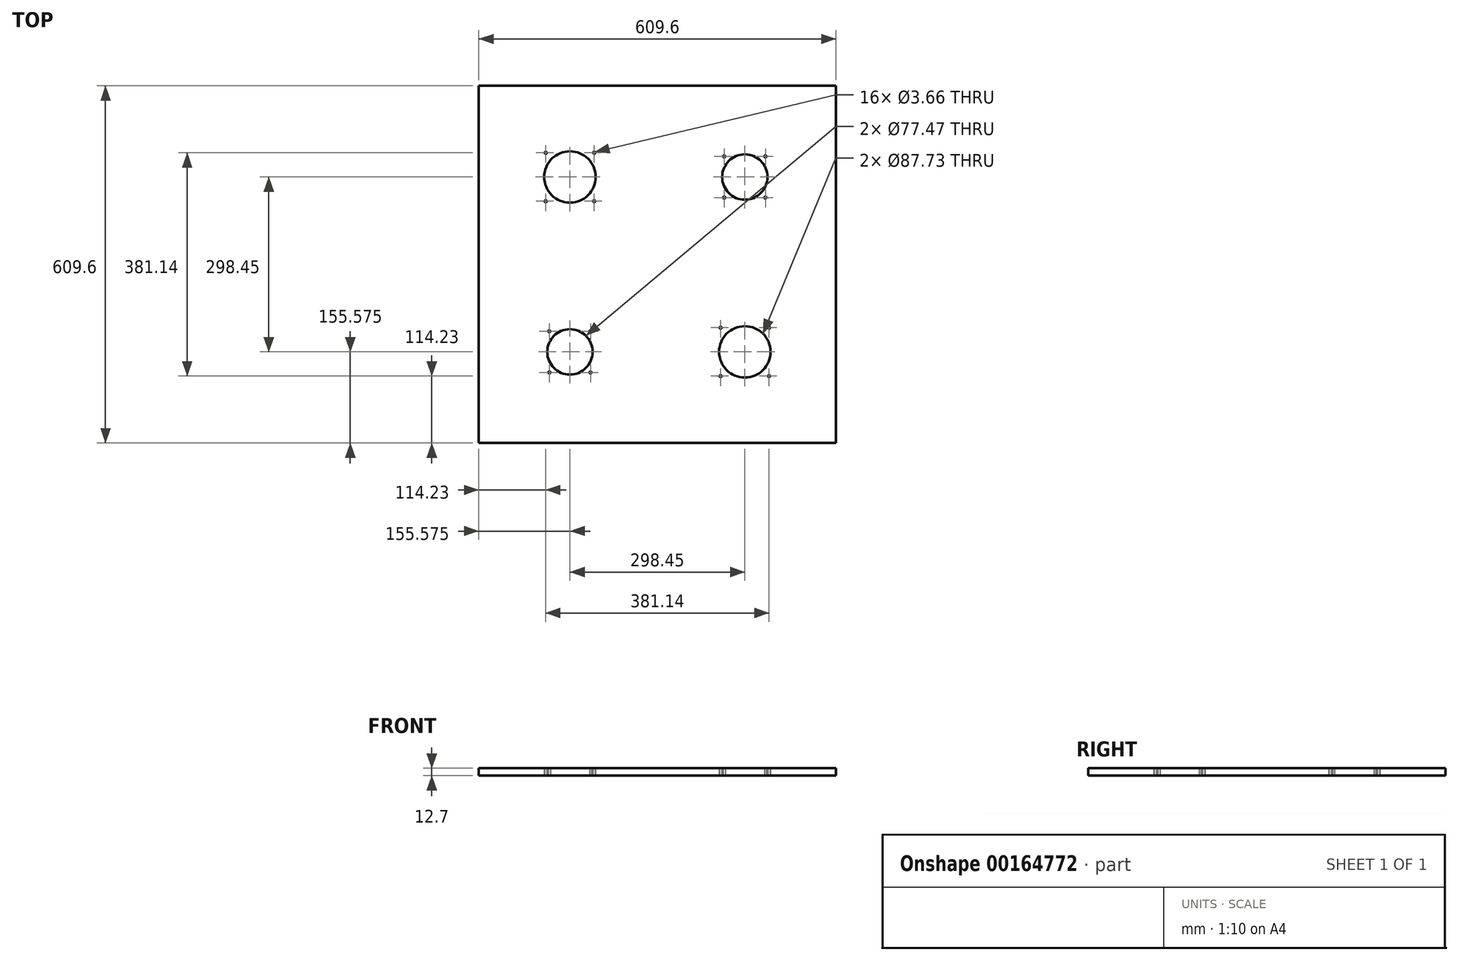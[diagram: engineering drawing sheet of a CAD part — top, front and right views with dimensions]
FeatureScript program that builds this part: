
annotation { "Feature Type Name" : "Feature", "Feature Type Description" : "" }
export const myFeature = defineFeature(function(context is Context, id is Id, definition is map)
    precondition{}
    {
        {
            var Q0;
            Q0=qCreatedBy(makeId("Top.planeOp"),FACE);
            var sketch = newSketch(context, id + "F0", { "sketchPlane" : qUnion([Q0])});
            skLineSegment(sketch, "E0.bottom", {"start": v(304.8, 304.8) * mm, "end": v(-304.8, 304.8) * mm});
            skLineSegment(sketch, "E0.top", {"start": v(304.8, -304.8) * mm, "end": v(-304.8, -304.8) * mm});
            skLineSegment(sketch, "E0.left", {"start": v(304.8, 304.8) * mm, "end": v(304.8, -304.8) * mm});
            skLineSegment(sketch, "E0.right", {"start": v(-304.8, 304.8) * mm, "end": v(-304.8, -304.8) * mm});
            skPoint(sketch, "E0.middle", {"position": v(0, 0) * mm});
            skLineSegment(sketch, "E1.bottom", {"start": v(6.35, 6.35) * mm, "end": v(-6.35, 6.35) * mm, "construction": true});
            skLineSegment(sketch, "E1.top", {"start": v(6.35, -6.35) * mm, "end": v(-6.35, -6.35) * mm, "construction": true});
            skLineSegment(sketch, "E1.left", {"start": v(6.35, 6.35) * mm, "end": v(6.35, -6.35) * mm, "construction": true});
            skLineSegment(sketch, "E1.right", {"start": v(-6.35, 6.35) * mm, "end": v(-6.35, -6.35) * mm, "construction": true});
            skLineSegment(sketch, "E2.bottom", {"start": v(6.35, 6.35) * mm, "end": v(292.1, 6.35) * mm, "construction": true});
            skLineSegment(sketch, "E2.top", {"start": v(6.35, 292.1) * mm, "end": v(292.1, 292.1) * mm, "construction": true});
            skLineSegment(sketch, "E2.left", {"start": v(6.35, 6.35) * mm, "end": v(6.35, 292.1) * mm, "construction": true});
            skLineSegment(sketch, "E2.right", {"start": v(292.1, 6.35) * mm, "end": v(292.1, 292.1) * mm, "construction": true});
            skLineSegment(sketch, "E3.bottom", {"start": v(-6.35, 6.35) * mm, "end": v(-292.1, 6.35) * mm, "construction": true});
            skLineSegment(sketch, "E3.top", {"start": v(-6.35, 292.1) * mm, "end": v(-292.1, 292.1) * mm, "construction": true});
            skLineSegment(sketch, "E3.left", {"start": v(-6.35, 6.35) * mm, "end": v(-6.35, 292.1) * mm, "construction": true});
            skLineSegment(sketch, "E3.right", {"start": v(-292.1, 6.35) * mm, "end": v(-292.1, 292.1) * mm, "construction": true});
            skLineSegment(sketch, "E4.bottom", {"start": v(-6.35, -6.35) * mm, "end": v(-292.1, -6.35) * mm, "construction": true});
            skLineSegment(sketch, "E4.top", {"start": v(-6.35, -292.1) * mm, "end": v(-292.1, -292.1) * mm, "construction": true});
            skLineSegment(sketch, "E4.left", {"start": v(-6.35, -6.35) * mm, "end": v(-6.35, -292.1) * mm, "construction": true});
            skLineSegment(sketch, "E4.right", {"start": v(-292.1, -6.35) * mm, "end": v(-292.1, -292.1) * mm, "construction": true});
            skLineSegment(sketch, "E5.bottom", {"start": v(6.35, -6.35) * mm, "end": v(292.1, -6.35) * mm, "construction": true});
            skLineSegment(sketch, "E5.top", {"start": v(6.35, -292.1) * mm, "end": v(292.1, -292.1) * mm, "construction": true});
            skLineSegment(sketch, "E5.left", {"start": v(6.35, -6.35) * mm, "end": v(6.35, -292.1) * mm, "construction": true});
            skLineSegment(sketch, "E5.right", {"start": v(292.1, -6.35) * mm, "end": v(292.1, -292.1) * mm, "construction": true});
            skLineSegment(sketch, "E6", {"start": v(-292.1, 292.1) * mm, "end": v(-304.8, 292.1) * mm, "construction": true});
            skLineSegment(sketch, "E7", {"start": v(-292.1, 292.1) * mm, "end": v(-292.1, 304.8) * mm, "construction": true});
            skLineSegment(sketch, "E8", {"start": v(-149.23, -6.35) * mm, "end": v(-149.22, -292.1) * mm, "construction": true});
            skLineSegment(sketch, "E9", {"start": v(149.22, -6.35) * mm, "end": v(149.22, -292.1) * mm, "construction": true});
            skLineSegment(sketch, "E10", {"start": v(-149.22, 6.35) * mm, "end": v(-149.22, 292.1) * mm, "construction": true});
            skLineSegment(sketch, "E11", {"start": v(149.22, 292.1) * mm, "end": v(149.22, 6.35) * mm, "construction": true});
            skCircle(sketch, "E12", {"center": v(-149.23, 149.22) * mm, "radius": 43.87 * mm});
            skCircle(sketch, "E13", {"center": v(149.22, 149.23) * mm, "radius": 38.73 * mm});
            skCircle(sketch, "E14", {"center": v(149.22, -149.22) * mm, "radius": 43.87 * mm});
            skCircle(sketch, "E15", {"center": v(-149.22, -149.22) * mm, "radius": 38.73 * mm});
            skLineSegment(sketch, "E16.bottom", {"start": v(-107.88, 107.88) * mm, "end": v(-190.57, 107.88) * mm, "construction": true});
            skLineSegment(sketch, "E16.top", {"start": v(-107.88, 190.57) * mm, "end": v(-190.57, 190.57) * mm, "construction": true});
            skLineSegment(sketch, "E16.left", {"start": v(-107.88, 107.88) * mm, "end": v(-107.88, 190.57) * mm, "construction": true});
            skLineSegment(sketch, "E16.right", {"start": v(-190.57, 107.88) * mm, "end": v(-190.57, 190.57) * mm, "construction": true});
            skLineSegment(sketch, "E17.bottom", {"start": v(114.07, 114.07) * mm, "end": v(184.38, 114.07) * mm, "construction": true});
            skLineSegment(sketch, "E17.top", {"start": v(114.07, 184.38) * mm, "end": v(184.38, 184.38) * mm, "construction": true});
            skLineSegment(sketch, "E17.left", {"start": v(114.07, 114.07) * mm, "end": v(114.07, 184.38) * mm, "construction": true});
            skLineSegment(sketch, "E17.right", {"start": v(184.38, 114.07) * mm, "end": v(184.38, 184.38) * mm, "construction": true});
            skLineSegment(sketch, "E18.bottom", {"start": v(190.57, -190.57) * mm, "end": v(107.88, -190.57) * mm, "construction": true});
            skLineSegment(sketch, "E18.top", {"start": v(190.57, -107.88) * mm, "end": v(107.88, -107.88) * mm, "construction": true});
            skLineSegment(sketch, "E18.left", {"start": v(190.57, -190.57) * mm, "end": v(190.57, -107.88) * mm, "construction": true});
            skLineSegment(sketch, "E18.right", {"start": v(107.88, -190.57) * mm, "end": v(107.88, -107.88) * mm, "construction": true});
            skLineSegment(sketch, "E19.bottom", {"start": v(-114.07, -184.38) * mm, "end": v(-184.38, -184.38) * mm, "construction": true});
            skLineSegment(sketch, "E19.top", {"start": v(-114.07, -114.07) * mm, "end": v(-184.38, -114.07) * mm, "construction": true});
            skLineSegment(sketch, "E19.left", {"start": v(-114.07, -184.38) * mm, "end": v(-114.07, -114.07) * mm, "construction": true});
            skLineSegment(sketch, "E19.right", {"start": v(-184.38, -184.38) * mm, "end": v(-184.38, -114.07) * mm, "construction": true});
            skCircle(sketch, "E20", {"center": v(-107.88, 190.57) * mm, "radius": 1.83 * mm});
            skCircle(sketch, "E21", {"center": v(-190.57, 190.57) * mm, "radius": 1.83 * mm});
            skCircle(sketch, "E22", {"center": v(-190.57, 107.88) * mm, "radius": 1.83 * mm});
            skCircle(sketch, "E23", {"center": v(-107.88, 107.88) * mm, "radius": 1.83 * mm});
            skCircle(sketch, "E24", {"center": v(114.07, 114.07) * mm, "radius": 1.83 * mm});
            skCircle(sketch, "E25", {"center": v(114.07, 184.38) * mm, "radius": 1.83 * mm});
            skCircle(sketch, "E26", {"center": v(184.38, 114.07) * mm, "radius": 1.83 * mm});
            skCircle(sketch, "E27", {"center": v(184.38, 184.38) * mm, "radius": 1.83 * mm});
            skCircle(sketch, "E28", {"center": v(-184.38, -114.07) * mm, "radius": 1.83 * mm});
            skCircle(sketch, "E29", {"center": v(-114.07, -114.07) * mm, "radius": 1.83 * mm});
            skCircle(sketch, "E30", {"center": v(-184.38, -184.38) * mm, "radius": 1.83 * mm});
            skCircle(sketch, "E31", {"center": v(-114.07, -184.38) * mm, "radius": 1.83 * mm});
            skCircle(sketch, "E32", {"center": v(107.88, -190.57) * mm, "radius": 1.83 * mm});
            skCircle(sketch, "E33", {"center": v(107.88, -107.88) * mm, "radius": 1.83 * mm});
            skCircle(sketch, "E34", {"center": v(190.57, -107.88) * mm, "radius": 1.83 * mm});
            skCircle(sketch, "E35", {"center": v(190.57, -190.57) * mm, "radius": 1.83 * mm});
            skSolve(sketch);
        }
        {
            var Q0;
            Q0=qSketchRegion(id+"F0",true);
            extrude(context, id + "F1", {"entities" : qUnion([Q0]), "depth" : 12.7 * mm});
        }
    });
